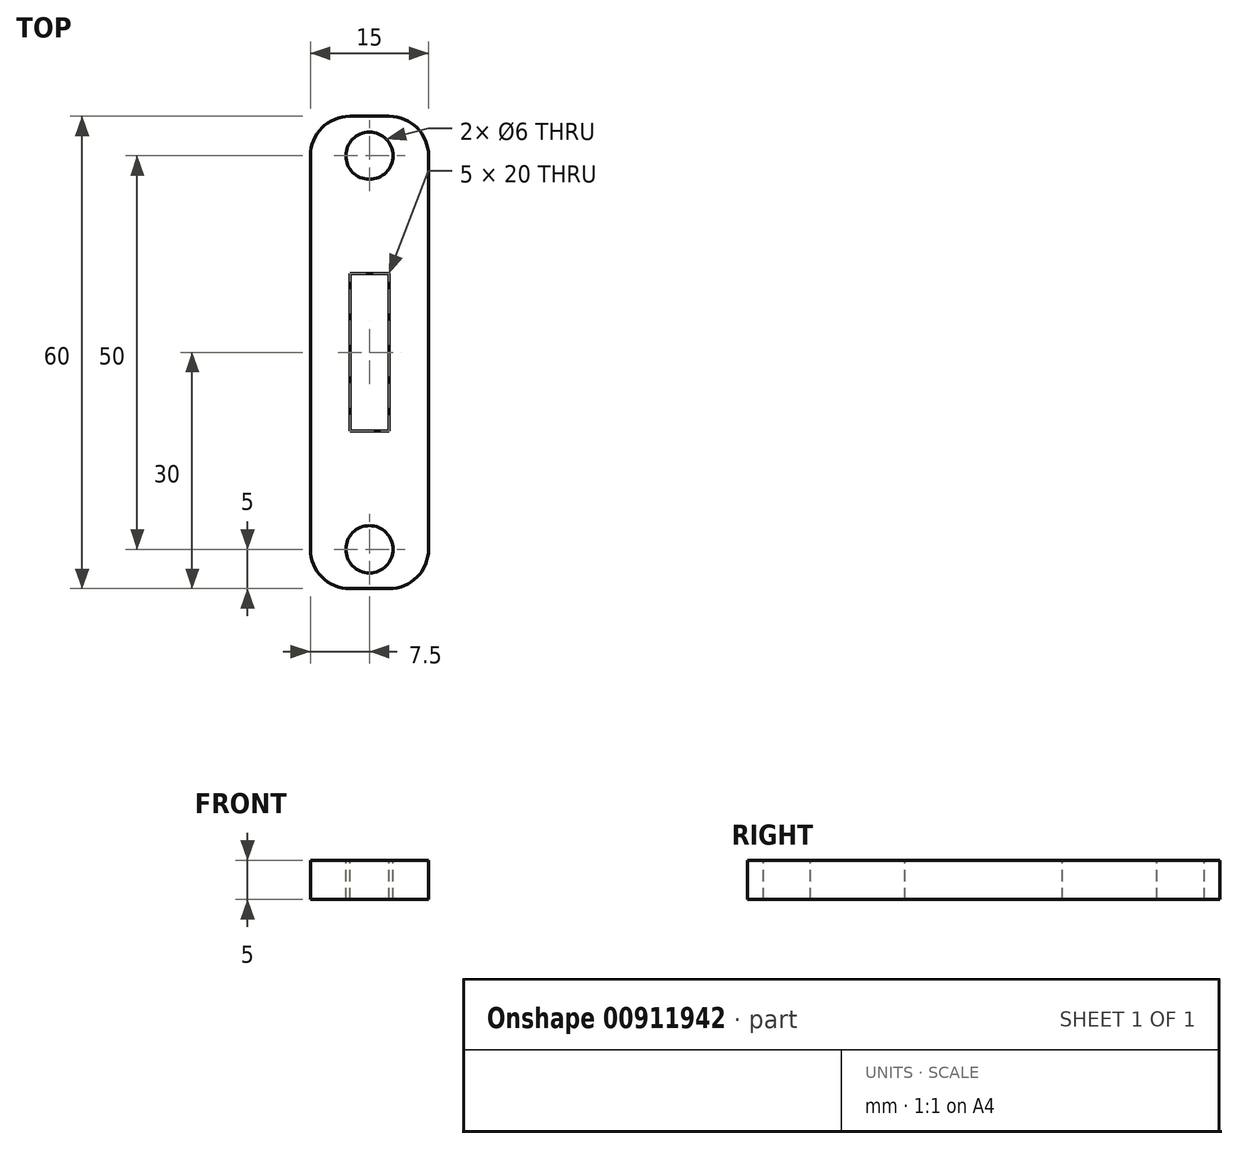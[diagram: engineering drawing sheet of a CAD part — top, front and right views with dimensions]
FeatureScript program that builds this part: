
annotation { "Feature Type Name" : "Feature", "Feature Type Description" : "" }
export const myFeature = defineFeature(function(context is Context, id is Id, definition is map)
    precondition{}
    {
        {
            var Q0;
            Q0=qCreatedBy(makeId("Top.planeOp"),FACE);
            var sketch = newSketch(context, id + "F0", { "sketchPlane" : qUnion([Q0])});
            skLineSegment(sketch, "E0.bottom", {"start": v(-7.5, -30) * mm, "end": v(7.5, -30) * mm});
            skLineSegment(sketch, "E0.top", {"start": v(-7.5, 30) * mm, "end": v(7.5, 30) * mm});
            skLineSegment(sketch, "E0.left", {"start": v(-7.5, -30) * mm, "end": v(-7.5, 30) * mm});
            skLineSegment(sketch, "E0.right", {"start": v(7.5, -30) * mm, "end": v(7.5, 30) * mm});
            skLineSegment(sketch, "E1", {"start": v(0, -30) * mm, "end": v(0, 30) * mm, "construction": true});
            skLineSegment(sketch, "E2", {"start": v(-7.5, 0) * mm, "end": v(7.5, 0) * mm, "construction": true});
            skSolve(sketch);
        }
        {
            var Q0;
            Q0 = qSketchRegion(id + "F0", true);
            extrude(context, id + "F1", {"entities" : qUnion([Q0]), "depth" : 5 * mm, "offsetDistance" : 25 * mm});
        }
        {
            var Q0;
            Q0=makeQuery(id+"F1.opExtrude","SWEPT_EDGE",EDGE,{"disambiguationData":[OSD([sQuery(id+"F0.wireOp",EDGE,"E0.bottom"),sQuery(id+"F0.wireOp",EDGE,"E0.right")])]});
            var Q1;
            Q1=makeQuery(id+"F1.opExtrude","SWEPT_EDGE",EDGE,{"disambiguationData":[OSD([sQuery(id+"F0.wireOp",EDGE,"E0.bottom"),sQuery(id+"F0.wireOp",EDGE,"E0.left")])]});
            var Q2;
            Q2=makeQuery(id+"F1.opExtrude","SWEPT_EDGE",EDGE,{"disambiguationData":[OSD([sQuery(id+"F0.wireOp",EDGE,"E0.top"),sQuery(id+"F0.wireOp",EDGE,"E0.right")])]});
            var Q3;
            Q3=makeQuery(id+"F1.opExtrude","SWEPT_EDGE",EDGE,{"disambiguationData":[OSD([sQuery(id+"F0.wireOp",EDGE,"E0.top"),sQuery(id+"F0.wireOp",EDGE,"E0.left")])]});
            fillet(context, id + "F2", {"entities" : qUnion([Q0, Q1, Q2, Q3]), "radius" : 5 * mm, "tangentPropagation" : true, "allowEdgeOverflow" : false});
        }
        {
            var Q0;
            Q0=makeQuery(id+"F1.opExtrude","CAP_FACE",FACE,{"disambiguationData":[OSD([sQuery(id+"F0.wireOp",EDGE,"E0.bottom"),sQuery(id+"F0.wireOp",EDGE,"E0.top"),sQuery(id+"F0.wireOp",EDGE,"E0.left"),sQuery(id+"F0.wireOp",EDGE,"E0.right")])],"isStart":false});
            var sketch = newSketch(context, id + "F3", { "sketchPlane" : qUnion([Q0])});
            skLineSegment(sketch, "E3", {"start": v(0, 30) * mm, "end": v(0, -30) * mm, "construction": true});
            skLineSegment(sketch, "E4", {"start": v(-7.5, 0) * mm, "end": v(7.5, 0) * mm, "construction": true});
            skCircle(sketch, "E5", {"center": v(0, -25) * mm, "radius": 3 * mm});
            skCircle(sketch, "E6", {"center": v(0, 25) * mm, "radius": 3 * mm});
            skSolve(sketch);
        }
        {
            var Q0;
            Q0=makeQuery(id+"F3.imprint","IMPRINT",FACE,{"disambiguationData":[TD([[makeQuery(id+"F3.imprint","IMPRINT",EDGE,{"derivedFrom":sQuery(id+"F3.wireOp",EDGE,"E5")}),-1.0]])]});
            var sketch = newSketch(context, id + "F4", { "sketchPlane" : qUnion([Q0])});
            skLineSegment(sketch, "E7.bottom", {"start": v(-2.5, 10) * mm, "end": v(2.5, 10) * mm});
            skLineSegment(sketch, "E7.top", {"start": v(-2.5, -10) * mm, "end": v(2.5, -10) * mm});
            skLineSegment(sketch, "E7.left", {"start": v(-2.5, 10) * mm, "end": v(-2.5, -10) * mm});
            skLineSegment(sketch, "E7.right", {"start": v(2.5, 10) * mm, "end": v(2.5, -10) * mm});
            skSolve(sketch);
        }
        {
            var Q0;
            Q0 = qSketchRegion(id + "F4", true);
            extrude(context, id + "F5", {"entities" : qUnion([Q0]), "operationType" : NewBodyOperationType.REMOVE, "endBound" : BoundingType.UP_TO_NEXT, "oppositeDirection" : true, "depth" : 40 * mm, "offsetDistance" : 25 * mm});
        }
        {
            var Q0;
            Q0 = qSketchRegion(id + "F3", true);
            extrude(context, id + "F6", {"entities" : qUnion([Q0]), "operationType" : NewBodyOperationType.REMOVE, "endBound" : BoundingType.UP_TO_NEXT, "oppositeDirection" : true, "depth" : 25 * mm, "offsetDistance" : 25 * mm});
        }
    });
